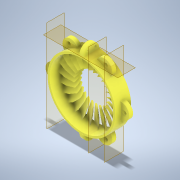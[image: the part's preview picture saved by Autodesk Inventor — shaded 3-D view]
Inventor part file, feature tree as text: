
AUTODESK INVENTOR PART (.ipt)
format: ipt  version: 2021.2 (Build 252289000, 289)  size: 885,248 bytes
history: native  units: in
note: dims shown in document units (in); Inventor stores cm internally (conversion verified against a paired STEP export)
features: sketch x9, extrude x8, plane x4, pattern_circular x3, fillet x2, loft x1, other x1
ambient origin geometry x8: Origin, YZ Plane, XZ Plane, XY Plane, X Axis, Y Axis, Z Axis, Center Point
bodies: Solid1 (feature_tree)
feature tree (28):
  extrude  "Extrusion1"  Depth=4.25in
  plane  "Work Plane2"
  extrude  "Extrusion3"  Depth=2.125in
  fillet  "Fillet1"  Radius=0.25in
  extrude  "Extrusion4"  Depth=0.5in TaperAngle=0.0deg
  pattern_circular  "Circular Pattern2"  Count=2 Angle=360.0deg
  plane  "Work Plane3"
  extrude  "Extrusion5"  Depth=1.0in
  extrude  "Extrusion6"  Depth=0.5in
  fillet  "Fillet2"  [1 undecoded]
  extrude  "Extrusion7"  Depth=0.1in TaperAngle=0.0deg
  pattern_circular  "Circular Pattern3"  [2 undecoded]
  plane  "Work Plane4"
  plane  "Work Plane6"
  sketch  "Sketch13"  dims[d18=0.5in d19=0.0in d20=0.7874in d21=360.0deg]
  extrude  "Extrusion15"  Depth=0.5in
  loft  "Loft5"
  pattern_circular  "Circular Pattern9"  [2 undecoded]
  extrude  "Extrusion16"  Depth=0.5in TaperAngle=0.0deg
  sketch  "Sketch1"  dims[d0=4.0in d1=4.25in]
  sketch  "Sketch3"  dims[d2=1.0in d3=0.0in d10=2.125in d11=0.25in]
  sketch  "Sketch4"  dims[d12=0.0in d13=0.5in d14=0.0in]
  sketch  "Sketch5"  dims[d15=0.5in]
  sketch  "Sketch6"  dims[d16=0.125in]
  sketch  "Sketch7"  dims[d17=0.2in]
  sketch  "Sketch16"  dims[d23=-2.125in d24=1.0in]
  other  "Edges5"
  sketch  "Sketch18"  dims[d25=0.25in d26=0.5in d27=0.0in d28=0.1in d29=0.0in d30=0.5in d31=0.0in d32=0.5in d33=0.25in d34=0.2in d35=0.5in d36=0.0in d37=2.3622in d38=360.0deg d40=0.25in d41=0.125in d42=0.25in d43=0.2in d49=0.5in d75=1.5in d111=0.5in d112=0.0312in d113=0.5in d114=0.0in d115=0.0in d116=90.0deg d117=0.0in d118=90.0deg d119=9.4488in d120=360.0deg d122=1.8625in d123=0.0in d124=0.0777in d79=0.5in d80=0.0344in d81=0.5in d82=0.0344in]
note: 5 required parameter values undecoded (feature->parameter linkage not recoverable at this tier; creation-order binding heuristic only, values carry confidence <= 0.55)
